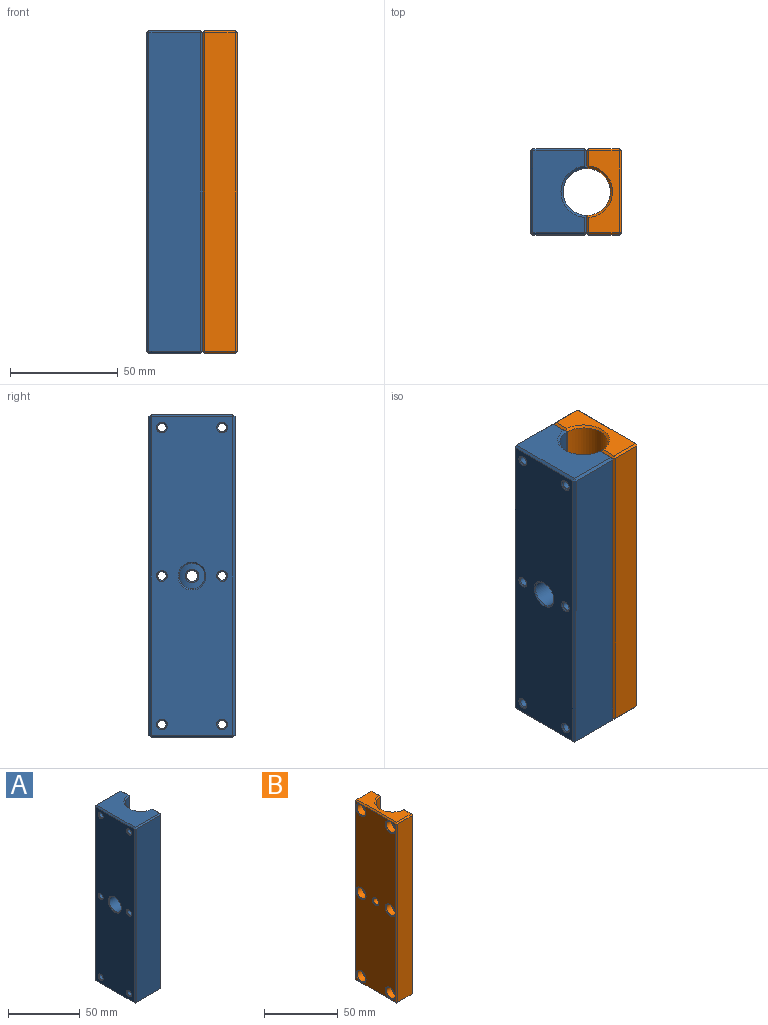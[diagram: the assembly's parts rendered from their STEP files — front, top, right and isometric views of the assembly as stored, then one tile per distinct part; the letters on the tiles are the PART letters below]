
ASSEMBLY  parts=2 mates=1
PART A: 58 faces, bbox 26x40x150 mm
  f0: cylinder r=11mm len=148mm, axis (0,0,-1), area 4943.9mm2, adj f17,f18,f21,f37,f40
  f1: plane 148x24mm, normal (0,1,0), area 3552mm2, adj f46,f51,f54,f57
  f2: plane 148x24mm, normal (0,-1,0), area 3552mm2, adj f35,f42,f43,f44
  f3: plane 148x7.51mm, normal (1,0,0), area 1052.7mm2, adj f17,f20,f22,f25,f34,f35,f36
  f4: plane 148x7.51mm, normal (1,0,0), area 1052.7mm2, adj f18,f19,f23,f24,f41,f45,f46
  f5: plane 38x24mm, normal (0,0,1), area 709.8mm2, adj f34,f37,f41,f42,f51,f52
  f6: plane 38x24mm, normal (0,0,-1), area 709.8mm2, adj f36,f40,f44,f45,f53,f54
  f7: cylinder r=2.6mm len=5.2mm, axis (-1,0,0), area 76.6mm2, adj f21,f29
  f8: cylinder r=2mm len=25mm, axis (-1,0,0), area 314.2mm2, adj f24,f33
  f9: cylinder r=2mm len=25mm, axis (-1,0,0), area 314.2mm2, adj f19,f27
  f10: cylinder r=2mm len=25mm, axis (-1,0,0), area 314.2mm2, adj f23,f31
  f11: cylinder r=2mm len=25mm, axis (-1,0,0), area 314.2mm2, adj f20,f26
  f12: cylinder r=2mm len=25mm, axis (-1,0,0), area 314.2mm2, adj f22,f28
  f13: cylinder r=2mm len=25mm, axis (-1,0,0), area 314.2mm2, adj f25,f32
  f14: plane 148x38mm, normal (-1,0,0), area 5373.5mm2, adj f26,f27,f28,f30,f31,f32,f33,f43
  f15: cylinder r=11mm len=12mm, axis (0,0,-1), area 86mm2, adj f16,f29
  f16: cylinder r=6mm len=12mm, axis (-1,0,0), area 339.3mm2, adj f15,f30
  f17: plane 148.48x0.5mm, normal (0.72,0.69,0), area 102.5mm2, adj f0,f3,f34,f36,f37,f40
  f18: plane 148.48x0.5mm, normal (0.72,-0.69,0), area 102.5mm2, adj f0,f4,f37,f40,f41,f45
  f19: cone r=2mm half-angle=45deg, axis (1,0,0), area 10mm2, adj f4,f9
  f20: cone r=2mm half-angle=45deg, axis (1,0,0), area 10mm2, adj f3,f11
  f21: bspline ~6.2x5.92mm, area 11.7mm2, adj f0,f7
  f22: cone r=2mm half-angle=45deg, axis (1,0,0), area 10mm2, adj f3,f12
  f23: cone r=2mm half-angle=45deg, axis (1,0,0), area 10mm2, adj f4,f10
  f24: cone r=2mm half-angle=45deg, axis (1,0,0), area 10mm2, adj f4,f8
  f25: cone r=2mm half-angle=45deg, axis (1,0,0), area 10mm2, adj f3,f13
  f26: cone r=2.5mm half-angle=45deg, axis (-1,0,0), area 10mm2, adj f11,f14
  f27: cone r=2.5mm half-angle=45deg, axis (-1,0,0), area 10mm2, adj f9,f14
  f28: cone r=2.5mm half-angle=45deg, axis (-1,0,0), area 10mm2, adj f12,f14
  f29: bspline ~6.5x6.2mm, area 13.8mm2, adj f7,f15
  f30: cone r=6mm half-angle=45deg, axis (-1,0,0), area 27.8mm2, adj f14,f16
  f31: cone r=2.5mm half-angle=45deg, axis (-1,0,0), area 10mm2, adj f10,f14
  f32: cone r=2.5mm half-angle=45deg, axis (-1,0,0), area 10mm2, adj f13,f14
  f33: cone r=2.5mm half-angle=45deg, axis (-1,0,0), area 10mm2, adj f8,f14
  f34: plane 7.78x1.02mm, normal (0.71,0,0.71), area 10.5mm2, adj f3,f5,f17,f37,f38
  f35: plane 148x1mm, normal (0.71,-0.71,0), area 209.3mm2, adj f2,f3,f38,f39
  f36: plane 7.78x1.02mm, normal (0.71,0,-0.71), area 10.5mm2, adj f3,f6,f17,f39,f40
  f37: cone r=11mm half-angle=45deg, axis (0,0,1), area 49.5mm2, adj f0,f5,f17,f18,f34,f41
  f38: plane 1x1mm, normal (0.58,-0.58,0.58), area 0.9mm2, adj f34,f35,f42
  f39: plane 1x1mm, normal (0.58,-0.58,-0.58), area 0.9mm2, adj f35,f36,f44
  f40: cone r=12mm half-angle=45deg, axis (0,0,-1), area 49.5mm2, adj f0,f6,f17,f18,f36,f45
  f41: plane 7.78x1.02mm, normal (0.71,0,0.71), area 10.5mm2, adj f4,f5,f18,f37,f47
  f42: plane 24x1mm, normal (0,-0.71,0.71), area 33.9mm2, adj f2,f5,f38,f48
  f43: plane 148x1mm, normal (-0.71,-0.71,0), area 209.3mm2, adj f2,f14,f48,f49
  f44: plane 24x1mm, normal (0,-0.71,-0.71), area 33.9mm2, adj f2,f6,f39,f49
  f45: plane 7.78x1.02mm, normal (0.71,0,-0.71), area 10.5mm2, adj f4,f6,f18,f40,f50
  f46: plane 148x1mm, normal (0.71,0.71,0), area 209.3mm2, adj f1,f4,f47,f50
  f47: plane 1x1mm, normal (0.58,0.58,0.58), area 0.9mm2, adj f41,f46,f51
  f48: plane 1x1mm, normal (-0.58,-0.58,0.58), area 0.9mm2, adj f42,f43,f52
  f49: plane 1x1mm, normal (-0.58,-0.58,-0.58), area 0.9mm2, adj f43,f44,f53
  f50: plane 1x1mm, normal (0.58,0.58,-0.58), area 0.9mm2, adj f45,f46,f54
  f51: plane 24x1mm, normal (0,0.71,0.71), area 33.9mm2, adj f1,f5,f47,f55
  f52: plane 38x1mm, normal (-0.71,0,0.71), area 53.7mm2, adj f5,f14,f48,f55
  f53: plane 38x1mm, normal (-0.71,0,-0.71), area 53.7mm2, adj f6,f14,f49,f56
  f54: plane 24x1mm, normal (0,0.71,-0.71), area 33.9mm2, adj f1,f6,f50,f56
  f55: plane 1x1mm, normal (-0.58,0.58,0.58), area 0.9mm2, adj f51,f52,f57
  f56: plane 1x1mm, normal (-0.58,0.58,-0.58), area 0.9mm2, adj f53,f54,f57
  f57: plane 148x1mm, normal (-0.71,0.71,0), area 209.3mm2, adj f1,f14,f55,f56
PART B: 73 faces, bbox 16x40x150 mm
  f0: cylinder r=11mm len=148mm, axis (0,0,-1), area 4943.9mm2, adj f30,f33,f66,f70,f72
  f1: plane 148x14mm, normal (0,1,0), area 2072mm2, adj f39,f44,f47,f50
  f2: plane 148x38mm, normal (-1,0,0), area 5159.5mm2, adj f36,f45,f46,f50,f51,f52,f54,f57
  f3: plane 148x14mm, normal (0,-1,0), area 2072mm2, adj f28,f35,f36,f37
  f4: plane 148x7.51mm, normal (1,0,0), area 1025.4mm2, adj f27,f28,f29,f68,f69,f70,f71
  f5: plane 148x7.51mm, normal (1,0,0), area 1025.4mm2, adj f34,f38,f39,f64,f65,f66,f67
  f6: plane 38x14mm, normal (0,0,1), area 329.8mm2, adj f27,f30,f34,f35,f44,f45
  f7: plane 38x14mm, normal (0,0,-1), area 329.8mm2, adj f29,f33,f37,f38,f46,f47
  f8: cylinder r=2.6mm len=5.2mm, axis (-1,0,0), area 72.3mm2, adj f51,f72
  f9: cylinder r=2.6mm len=9.5mm, axis (-1,0,0), area 155.2mm2, adj f61,f67
  f10: cylinder r=2.6mm len=9.5mm, axis (-1,0,0), area 155.2mm2, adj f55,f64
  f11: cylinder r=2.6mm len=9.5mm, axis (-1,0,0), area 155.2mm2, adj f58,f65
  f12: cylinder r=2.6mm len=9.5mm, axis (-1,0,0), area 155.2mm2, adj f53,f69
  f13: cylinder r=2.6mm len=9.5mm, axis (-1,0,0), area 155.2mm2, adj f56,f68
  f14: cylinder r=2.6mm len=9.5mm, axis (-1,0,0), area 155.2mm2, adj f60,f71
  f15: cylinder r=4.3mm len=8.6mm, axis (-1,0,0), area 135.1mm2, adj f16,f63
  f16: plane 8.6x8.6mm, normal (-1,0,0), area 27.9mm2, adj f15,f60
  f17: cylinder r=4.3mm len=8.6mm, axis (-1,0,0), area 135.1mm2, adj f18,f57
  f18: plane 8.6x8.6mm, normal (-1,0,0), area 27.9mm2, adj f17,f56
  f19: cylinder r=4.3mm len=8.6mm, axis (-1,0,0), area 135.1mm2, adj f20,f52
  f20: plane 8.6x8.6mm, normal (-1,0,0), area 27.9mm2, adj f19,f53
  f21: cylinder r=4.3mm len=8.6mm, axis (-1,0,0), area 135.1mm2, adj f22,f59
  f22: plane 8.6x8.6mm, normal (-1,0,0), area 27.9mm2, adj f21,f58
  f23: cylinder r=4.3mm len=8.6mm, axis (-1,0,0), area 135.1mm2, adj f24,f54
  f24: plane 8.6x8.6mm, normal (-1,0,0), area 27.9mm2, adj f23,f55
  f25: cylinder r=4.3mm len=8.6mm, axis (-1,0,0), area 135.1mm2, adj f26,f62
  f26: plane 8.6x8.6mm, normal (-1,0,0), area 27.9mm2, adj f25,f61
  f27: plane 7.78x1.02mm, normal (0.71,0,0.71), area 10.5mm2, adj f4,f6,f30,f31,f70
  f28: plane 148x1mm, normal (0.71,-0.71,0), area 209.3mm2, adj f3,f4,f31,f32
  f29: plane 7.78x1.02mm, normal (0.71,0,-0.71), area 10.5mm2, adj f4,f7,f32,f33,f70
  f30: cone r=11mm half-angle=45deg, axis (0,0,1), area 49.5mm2, adj f0,f6,f27,f34,f66,f70
  f31: plane 1x1mm, normal (0.58,-0.58,0.58), area 0.9mm2, adj f27,f28,f35
  f32: plane 1x1mm, normal (0.58,-0.58,-0.58), area 0.9mm2, adj f28,f29,f37
  f33: cone r=12mm half-angle=45deg, axis (0,0,-1), area 49.5mm2, adj f0,f7,f29,f38,f66,f70
  f34: plane 7.78x1.02mm, normal (0.71,0,0.71), area 10.5mm2, adj f5,f6,f30,f40,f66
  f35: plane 14x1mm, normal (0,-0.71,0.71), area 19.8mm2, adj f3,f6,f31,f41
  f36: plane 148x1mm, normal (-0.71,-0.71,0), area 209.3mm2, adj f2,f3,f41,f42
  f37: plane 14x1mm, normal (0,-0.71,-0.71), area 19.8mm2, adj f3,f7,f32,f42
  f38: plane 7.78x1.02mm, normal (0.71,0,-0.71), area 10.5mm2, adj f5,f7,f33,f43,f66
  f39: plane 148x1mm, normal (0.71,0.71,0), area 209.3mm2, adj f1,f5,f40,f43
  f40: plane 1x1mm, normal (0.58,0.58,0.58), area 0.9mm2, adj f34,f39,f44
  f41: plane 1x1mm, normal (-0.58,-0.58,0.58), area 0.9mm2, adj f35,f36,f45
  f42: plane 1x1mm, normal (-0.58,-0.58,-0.58), area 0.9mm2, adj f36,f37,f46
  f43: plane 1x1mm, normal (0.58,0.58,-0.58), area 0.9mm2, adj f38,f39,f47
  f44: plane 14x1mm, normal (0,0.71,0.71), area 19.8mm2, adj f1,f6,f40,f48
  f45: plane 38x1mm, normal (-0.71,0,0.71), area 53.7mm2, adj f2,f6,f41,f48
  f46: plane 38x1mm, normal (-0.71,0,-0.71), area 53.7mm2, adj f2,f7,f42,f49
  f47: plane 14x1mm, normal (0,0.71,-0.71), area 19.8mm2, adj f1,f7,f43,f49
  f48: plane 1x1mm, normal (-0.58,0.58,0.58), area 0.9mm2, adj f44,f45,f50
  f49: plane 1x1mm, normal (-0.58,0.58,-0.58), area 0.9mm2, adj f46,f47,f50
  f50: plane 148x1mm, normal (-0.71,0.71,0), area 209.3mm2, adj f1,f2,f48,f49
  f51: cone r=3.1mm half-angle=45deg, axis (-1,0,0), area 12.7mm2, adj f2,f8
  f52: cone r=4.8mm half-angle=45deg, axis (-1,0,0), area 20.2mm2, adj f2,f19
  f53: cone r=3.1mm half-angle=45deg, axis (-1,0,0), area 12.7mm2, adj f12,f20
  f54: cone r=4.8mm half-angle=45deg, axis (-1,0,0), area 20.2mm2, adj f2,f23
  f55: cone r=3.1mm half-angle=45deg, axis (-1,0,0), area 12.7mm2, adj f10,f24
  f56: cone r=3.1mm half-angle=45deg, axis (-1,0,0), area 12.7mm2, adj f13,f18
  f57: cone r=4.8mm half-angle=45deg, axis (-1,0,0), area 20.2mm2, adj f2,f17
  f58: cone r=3.1mm half-angle=45deg, axis (-1,0,0), area 12.7mm2, adj f11,f22
  f59: cone r=4.8mm half-angle=45deg, axis (-1,0,0), area 20.2mm2, adj f2,f21
  f60: cone r=3.1mm half-angle=45deg, axis (-1,0,0), area 12.7mm2, adj f14,f16
  f61: cone r=3.1mm half-angle=45deg, axis (-1,0,0), area 12.7mm2, adj f9,f26
  f62: cone r=4.8mm half-angle=45deg, axis (-1,0,0), area 20.2mm2, adj f2,f25
  f63: cone r=4.8mm half-angle=45deg, axis (-1,0,0), area 20.2mm2, adj f2,f15
  f64: cone r=2.6mm half-angle=45deg, axis (1,0,0), area 11.6mm2, adj f5,f10,f66
  f65: cone r=2.6mm half-angle=45deg, axis (1,0,0), area 11.6mm2, adj f5,f11,f66
  f66: plane 148.48x0.5mm, normal (0.72,-0.69,0), area 99.5mm2, adj f0,f5,f30,f33,f34,f38,f64,f65
  f67: cone r=2.6mm half-angle=45deg, axis (1,0,0), area 11.6mm2, adj f5,f9,f66
  f68: cone r=2.6mm half-angle=45deg, axis (1,0,0), area 11.6mm2, adj f4,f13,f70
  f69: cone r=2.6mm half-angle=45deg, axis (1,0,0), area 11.6mm2, adj f4,f12,f70
  f70: plane 148.48x0.5mm, normal (0.72,0.69,0), area 99.5mm2, adj f0,f4,f27,f29,f30,f33,f68,f69
  f71: cone r=2.6mm half-angle=45deg, axis (1,0,0), area 11.6mm2, adj f4,f14,f70
  f72: bspline ~6.2x5.92mm, area 11.7mm2, adj f0,f8
PLACE A t=(-32.97,-22.78,-7.9)mm
PLACE B rot(axis=(0,-1,0),180deg) t=(-0.97,-22.78,-7.9)mm
MATE fastened A.f25 <-> B.f52  axis (1,0,0) through (-16.97,-56.78,-76.9)mm
